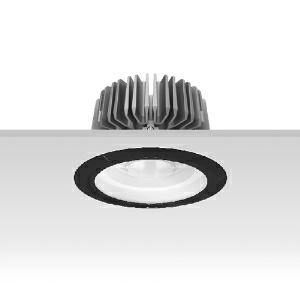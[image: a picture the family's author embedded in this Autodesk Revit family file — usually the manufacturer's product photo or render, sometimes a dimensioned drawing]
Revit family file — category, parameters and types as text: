
# Revit family: 3f_filippi_-_3f_reno_bianco_ampio_3f_filippi_-_30366_a01024_-_3f_reno_150_wh_3000-840_ep_wide___vt_bk_83ac
name_source: partatom
category: Lighting Fixtures
units: mm (PartAtom-declared; Revit-internal decimal feet)

## family parameters
Cut with Voids When Loaded = No
Host = Face
Light Source = No
Part Type = Normal
Room Calculation Point = No
Round Connector Dimension = Use Diameter
Shared = No

## types (1)
- 3F Filippi - 3F Reno Bianco Ampio (1 x LED, 2647 lm, 29 W, 4000 K)
    Apparent Load = 29 VA
    Approval mark = ENEC
    CIE Flux Codes = 74 93 99 100 100
    Color Rendering = 80
    Color Temperature = 4000 K
    Control Gear = Electronic ballast
    Default Elevation = 1800 mm
    Description = ILLUMINOTECHNICAL
Luminous efficiency 100% (DLOR 100%, ULOR 0%).
Initial luminous flux of the luminaire 2647 lm.
Emergency luminaire luminous flux BLF 14.3%.
Direct symmetric wide distribution.
Installation Interdistance Transv.D = 1.54 x hu - Long.D = 1.54 x hu.
Tabular UGR (CIE 117 - 4H-8H; S=0.25H; 70/50/20): RUG 24.4 - 24.2.
Beam angle: 74° - 73°.
Luminous efficacy 91 lm/W.
Lifetime (L90/B10): 30000 h. (tq+25°C)
Lifetime (L85/B10): 50000 h. (tq+25°C)
Lifetime (L70/B10): 80000 h. (tq+25°C)
Sudden decreased luminous flux after 50000 hours: 0% (C0).
Photobiological safety in compliance with IEC/TR 62778: RG0 risk exempt, (IEC 62471).
In compliance with IEC/EN 62722-2-1 - IEC/EN 62717 standards.

SOURCE
Compact LED module 3000/840.
Energy efficiency class (UE 2019/2020 - UE 2019/2015): D.
CIE 13.3 Colour rendering index: CRI >80 (R9 <50%).
IES TM-30 Fidelity Index: Rf = 84 Rg = 95.
CCT nominal colour temperature 4000 K.
Colour initial tolerance (MacAdam): SDCM 3.
Zhaga Book 3 compliant.

MECHANICAL
Passive heat dissipator in die-casting aluminium, oversized, for optimum thermal management of the LED module.
Parabolic element with graduated/concentric rings in white polycarbonate.
Transparent external lens with glossy and satin differentiated surfaces, with a cooling and anti-insect system in methacrylate (PMMA).
Fastening spring clips in stainless steel.
Dimensions: diameter 176 mm, height 111 mm. Weight 2 kg.
IP44 protection degree for exposed part, IP20 for recessed part.
Mechanical strength to impacts IK06 (1 joule).
Glow-wire test resistance 650°C.

ELECTRICAL
Wiring on a separate unit.
Halogen Free electronic wiring 230V-50/60Hz, power factor 0.90, THD <25%, constant output current, SELV, class II, 1 driver.
Power of the luminaire 29 W.
CE - IEC 60598-1 - EN 60598-1.
EP maintained emergency wiring on board, 1h duration, 24h recharge; compliant with EN 60598-2-22, excluding high risk areas.
SAFE FLICKER: PstLM=<1 and SVM=<0.4 (IEC TR 61547-1 and IEC TR 63158), to ensure a more comfortable and safe light.
Ambient temperature from +5°C to +25°C.
Temperature class T6 max 85°C.
Relative humidity UR: <85%.

INSTALLATION
Pull-up recessed fitting.
False ceiling carving: 150 mm.
All accessories dedicated to this product are available on the Catalog and on our website www.3F-Filippi.com.

ACCESSORIES
A01024 - VT transparent glass, tempered, not flammable, locked and in line with the trim, in black polycarbonate.

APPLICATIONS
Environments: architectural, commercial, exhibition areas, transit areas, corridors, shops, display windows, service areas.
In false ceilings with narrow voids.

WARNING
Luminaire designed for disposal/recycling at end-of-life.
Replaceable (LED only) light source by a professional. Replaceable control gear by a professional.
    Height = 0 mm  [stored 0 ft]
    Lamp = 1 x LED
    Lamp Light Flux = 2647 lm
    Lamp Power = 29 W
    Lamp count = 1
    Length = 176 mm
    Lifetime = 50000 h
    Luminous efficacy = 91 lm/W
    Manufacturer = 3F Filippi
    ModVariant = No
    Model = 3F Filippi - 30366+A01024 - 3F Reno 150 WH 3000-840 EP WIDE + VT BK
    Mounting Place = Ceiling
    Mounting Type = Recessed
    Number of Poles = 1
    OnlyDefault = Yes
    Power Factor = 1
    Product Name = 3F Filippi - 3F Reno Bianco Ampio
    Product group = recessed luminaire
    ProductGroupID = 4
    Protection Class = Protection class II
    Protection Degree = IP 20
    RLX_Detail_Level = 1
    RLX_Emergency_Light_Flux = 0 lm
    RLX_Emergency_Type = 0
    RLX_Emergency_Type_DB = No
    RlxData = <blob elided: 88029 chars, md5=66f8cbc6>
    Socket = socket
    Standby Power = 0 W
    System Light Flux = 2647 lm
    System Power = 29 W
    Type Comments = Product without accessories
    Type Image = 3ffilippi_3f_reno_150_wh_d150__a01024.jpg
    URL = http://relux.com
    VarID = ---
    Voltage = 0 V
    Weight = 0.00 kg
    Width = 0 mm  [stored 0 ft]

note: [stored X ft] marks values corroborated as IEEE doubles in the binary element streams (Revit-internal decimal feet)

## geometry (parser evidence)
native form markers: Blend x4, Sweep x11
no freeform markers — native parametric forms only
